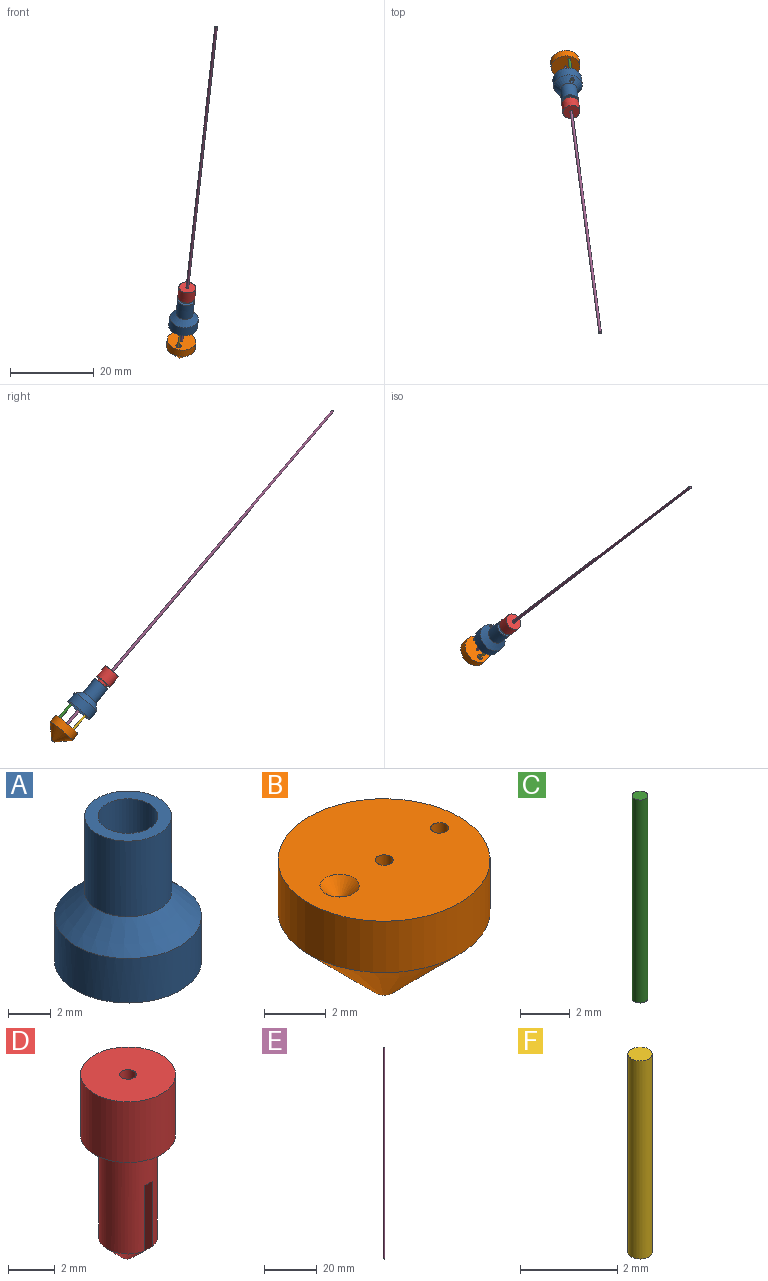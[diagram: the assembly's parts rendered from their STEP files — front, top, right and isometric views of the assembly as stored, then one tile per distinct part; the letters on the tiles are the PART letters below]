
ASSEMBLY  parts=6 mates=6
PART A: 11 faces, bbox 6.9x6.9x8.3 mm
  f0: cylinder r=0.36mm len=2.92mm, axis (0,0,-1), area 6.5mm2, adj f3,f9
  f1: cone r=0.89mm half-angle=45deg, axis (0,0,-1), area 32.8mm2, adj f2,f6,f10
  f2: cylinder r=3.43mm len=6.86mm, axis (0,0,-1), area 54.7mm2, adj f1,f3
  f3: plane 6.86x6.86mm, normal (0,0,-1), area 34.5mm2, adj f0,f2,f5,f10
  f4: plane 0.25x0.25mm, normal (0,0,-1), area 0.1mm2, adj f5
  f5: cone r=0.13mm half-angle=45deg, axis (0,0,-1), area 1.7mm2, adj f3,f4
  f6: cylinder r=2.03mm len=4.32mm, axis (0,0,-1), area 55mm2, adj f1,f7
  f7: plane 4.06x4.06mm, normal (0,0,1), area 6.8mm2, adj f6,f8
  f8: cylinder r=1.4mm len=4.29mm, axis (0,0,1), area 37.7mm2, adj f7,f9
  f9: cone r=1.88mm half-angle=45deg, axis (0,0,1), area 8.1mm2, adj f0,f8
  f10: cylinder r=0.51mm len=3.94mm, axis (0,0,-1), area 10.9mm2, adj f1,f3
PART B: 8 faces, bbox 6.9x6.9x5.1 mm
  f0: cylinder r=3.43mm len=6.86mm, axis (0,0,-1), area 43.8mm2, adj f1,f3
  f1: plane 6.86x6.86mm, normal (0,0,1), area 35.1mm2, adj f0,f4,f6,f7
  f2: plane 0.76x0.76mm, normal (0,0,-1), area 0.2mm2, adj f3,f4
  f3: cone r=3.43mm half-angle=45deg, axis (0,0,1), area 51.2mm2, adj f0,f2,f7
  f4: cylinder r=0.29mm len=5.08mm, axis (0,0,1), area 9.3mm2, adj f1,f2
  f5: plane 0.25x0.25mm, normal (0,0,1), area 0.1mm2, adj f6
  f6: cone r=0.13mm half-angle=45deg, axis (0,0,1), area 1.7mm2, adj f1,f5
  f7: cylinder r=0.29mm len=3.21mm, axis (0,0,1), area 5.3mm2, adj f1,f3
PART C: 3 faces, bbox 0.6x0.6x10 mm
  f0: cylinder r=0.32mm len=10mm, axis (0,0,-1), area 19.9mm2, adj f1,f2
  f1: plane 0.64x0.64mm, normal (0,0,1), area 0.3mm2, adj f0
  f2: plane 0.64x0.64mm, normal (0,0,-1), area 0.3mm2, adj f0
PART D: 13 faces, bbox 4.3x4.3x9.6 mm
  f0: cone r=1.25mm half-angle=45deg, axis (0,0,1), area 2.4mm2, adj f1,f5,f8,f12
  f1: cylinder r=1.25mm len=5.33mm, axis (0,0,-1), area 38.7mm2, adj f0,f4,f6,f7,f8,f9,f10,f11
  f2: cylinder r=2.03mm len=4.06mm, axis (0,0,-1), area 40.5mm2, adj f3,f4
  f3: plane 4.06x4.06mm, normal (0,0,1), area 12.5mm2, adj f2,f5
  f4: plane 4.06x4.06mm, normal (0,0,-1), area 8mm2, adj f1,f2
  f5: cylinder r=0.36mm len=9.4mm, axis (0,0,1), area 16.9mm2, adj f0,f3,f6,f7,f8,f9,f10,f11
  f6: cone r=1.25mm half-angle=45deg, axis (0,0,1), area 2.4mm2, adj f1,f5,f7,f11
  f7: plane 4.55x1.18mm, normal (-1,0,0), area 3.7mm2, adj f1,f5,f6,f9
  f8: plane 4.55x1.18mm, normal (1,0,0), area 3.7mm2, adj f0,f1,f5,f9
  f9: plane 0.97x0.45mm, normal (0,0,-1), area 0.4mm2, adj f1,f5,f7,f8
  f10: plane 0.97x0.45mm, normal (0,0,-1), area 0.4mm2, adj f1,f5,f11,f12
  f11: plane 4.55x1.18mm, normal (-1,0,0), area 3.7mm2, adj f1,f5,f6,f10
  f12: plane 4.55x1.18mm, normal (1,0,0), area 3.7mm2, adj f0,f1,f5,f10
PART E: 3 faces, bbox 0.6x0.6x98.4 mm
  f0: cylinder r=0.32mm len=98.43mm, axis (0,0,-1), area 196.3mm2, adj f1,f2
  f1: plane 0.64x0.64mm, normal (0,0,1), area 0.3mm2, adj f0
  f2: plane 0.64x0.64mm, normal (0,0,-1), area 0.3mm2, adj f0
PART F: 3 faces, bbox 0.5x0.5x5 mm
  f0: cylinder r=0.25mm len=5mm, axis (0,0,-1), area 7.9mm2, adj f1,f2
  f1: plane 0.5x0.5mm, normal (0,0,1), area 0.2mm2, adj f0
  f2: plane 0.5x0.5mm, normal (0,0,-1), area 0.2mm2, adj f0
PLACE A rot(axis=(0.47,-0.25,0.85),80.9deg) t=(-16.89,9.16,-21.65)mm
PLACE B rot(axis=(0.47,-0.25,0.85),80.9deg) t=(-17.69,15.34,-28.94)mm
PLACE C rot(axis=(0.88,0.26,-0.4),44.4deg) t=(-16.61,15.57,-25.52)mm
PLACE D rot(axis=(0.88,0.26,-0.4),44.4deg) t=(-17.36,12.76,-25.89)mm
PLACE E rot(axis=(0.47,-0.25,0.85),80.9deg) t=(-17.27,12.07,-25.08)mm fixed
PLACE F rot(axis=(0.88,0.26,-0.4),44.4deg) t=(-17.99,10.77,-26.5)mm
MATE slider A.f5 <-> F.f0  axis (-0.08,0.64,-0.76) through (-17.59,7.67,-22.84)mm
MATE revolute B.f4 <-> E.f0  axis (0.08,-0.64,0.76) through (-17.27,12.07,-25.08)mm
MATE slider A.f0 <-> E.f0  axis (-0.08,0.64,-0.76) through (-16.89,9.16,-21.65)mm
MATE revolute F.f0 <-> B.f6  axis (-0.08,0.64,-0.76) through (-17.99,10.77,-26.5)mm
MATE slider D.f5 <-> E.f0  axis (0.08,-0.64,0.76) through (-15.87,1.3,-12.37)mm
MATE revolute C.f0 <-> B.f7  axis (-0.08,0.64,-0.76) through (-16.61,15.57,-25.52)mm
